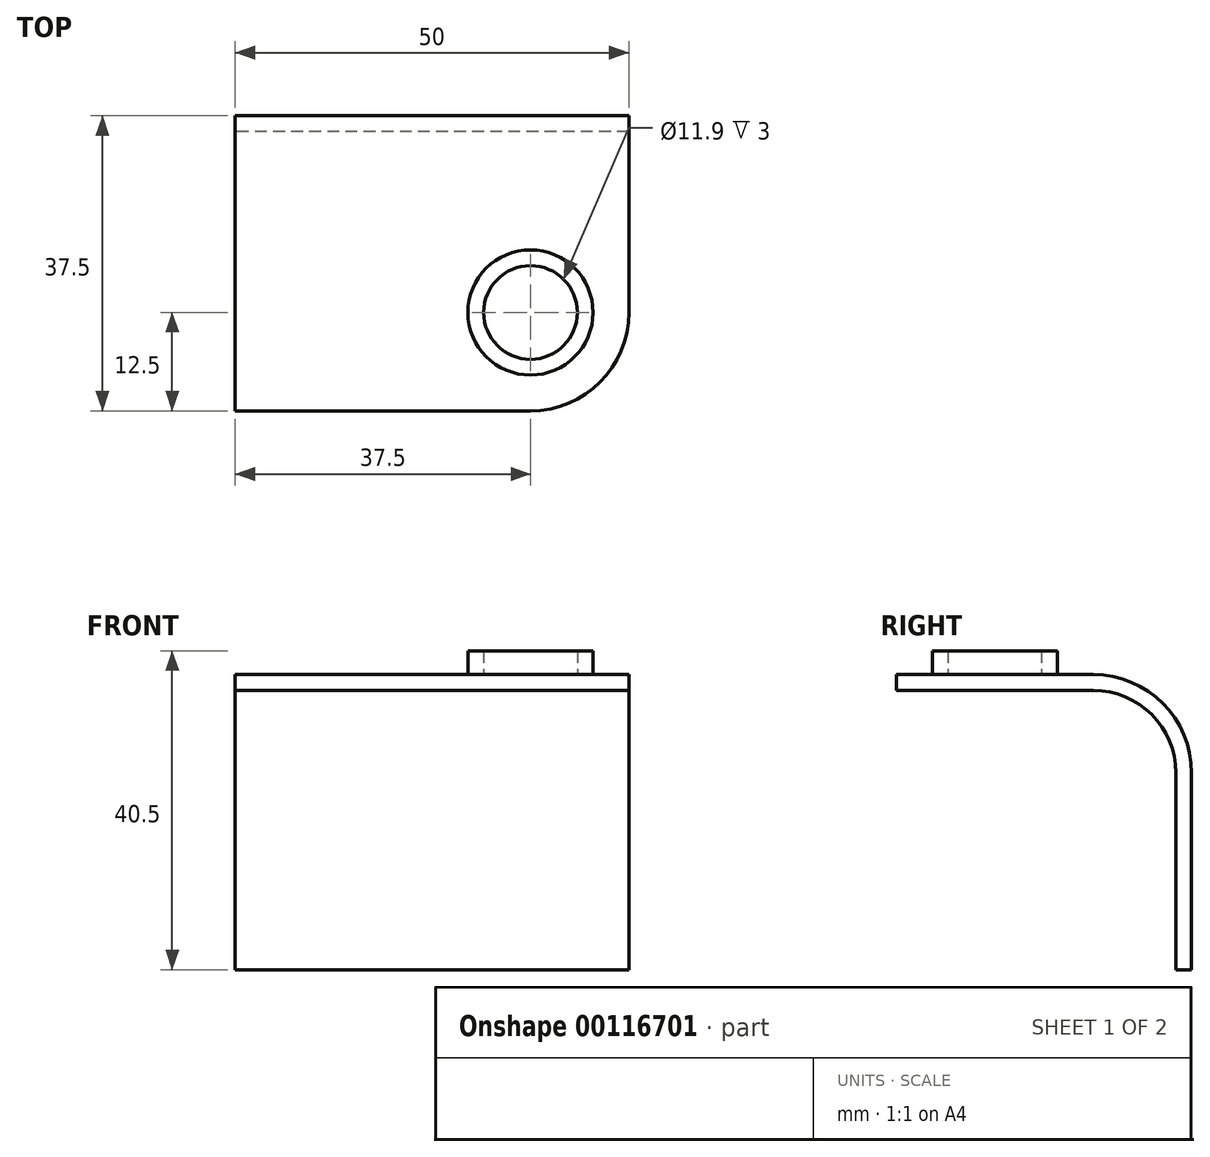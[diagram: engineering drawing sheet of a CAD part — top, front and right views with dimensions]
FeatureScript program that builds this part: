
annotation { "Feature Type Name" : "Feature", "Feature Type Description" : "" }
export const myFeature = defineFeature(function(context is Context, id is Id, definition is map)
    precondition{}
    {
        {
            var Q0;
            Q0=qCreatedBy(makeId("Front.planeOp"),FACE);
            var sketch = newSketch(context, id + "F0", { "sketchPlane" : qUnion([Q0])});
            skLineSegment(sketch, "E0.bottom", {"start": v(0, 0) * mm, "end": v(-50, 0) * mm});
            skLineSegment(sketch, "E0.top", {"start": v(0, 25) * mm, "end": v(-50, 25) * mm});
            skLineSegment(sketch, "E0.left", {"start": v(0, 0) * mm, "end": v(0, 25) * mm});
            skLineSegment(sketch, "E0.right", {"start": v(-50, 0) * mm, "end": v(-50, 25) * mm});
            skSolve(sketch);
        }
        {
            var Q0;
            Q0 = qSketchRegion(id + "F0", true);
            extrude(context, id + "F1", {"entities" : qUnion([Q0]), "depth" : 2 * mm});
        }
        {
            var Q0;
            Q0=qCreatedBy(makeId("Right.planeOp"),FACE);
            var sketch = newSketch(context, id + "F2", { "sketchPlane" : qUnion([Q0])});
            skArc(sketch, "E1", {"start": v(0, 25) * mm, "mid": v(-3.66, 33.84) * mm, "end": v(-12.5, 37.5) * mm});
            skLineSegment(sketch, "E2", {"start": v(-12.5, 37.5) * mm, "end": v(-37.5, 37.5) * mm});
            skLineSegment(sketch, "E3.0", {"start": v(-12.5, 35.5) * mm, "end": v(-37.5, 35.5) * mm});
            skArc(sketch, "E3.1", {"start": v(-2, 25) * mm, "mid": v(-5.08, 32.42) * mm, "end": v(-12.5, 35.5) * mm});
            skLineSegment(sketch, "E4", {"start": v(0, 25) * mm, "end": v(-2, 25) * mm});
            skLineSegment(sketch, "E5", {"start": v(-37.5, 37.5) * mm, "end": v(-37.5, 35.5) * mm});
            skSolve(sketch);
        }
        {
            var Q0;
            Q0=makeQuery(id+"F2.imprint","IMPRINT",FACE,{"disambiguationData":[TD([[makeQuery(id+"F2.imprint","IMPRINT",EDGE,{"derivedFrom":sQuery(id+"F2.wireOp",EDGE,"E1")}),1.0]])]});
            var Q1;
            Q1=makeQuery(id+"F1.opExtrude","SWEPT_FACE",FACE,{"disambiguationData":[OSD([sQuery(id+"F0.wireOp",EDGE,"E0.right")])]});
            extrude(context, id + "F3", {"entities" : qUnion([Q0]), "operationType" : NewBodyOperationType.ADD, "endBound" : BoundingType.UP_TO_SURFACE, "oppositeDirection" : true, "endBoundEntityFace" : qUnion([Q1]), "depth" : 25 * mm});
        }
        {
            var Q0;
            Q0=makeQuery(id+"F3.opExtrude","TWEAK_EDGE",EDGE,{"derivedFrom":[makeQuery(id+"F1.opExtrude","SWEPT_FACE",FACE,{"disambiguationData":[OSD([sQuery(id+"F0.wireOp",EDGE,"E0.right")])]}),makeQuery(id+"F2.imprint","IMPRINT",EDGE,{"derivedFrom":sQuery(id+"F2.wireOp",EDGE,"E5")})]});
            var Q1;
            Q1=makeQuery(id+"F3.opExtrude","CAP_EDGE",EDGE,{"disambiguationData":[OSD([sQuery(id+"F2.wireOp",EDGE,"E5")])],"isStart":true});
            fillet(context, id + "F4", {"entities" : qUnion([Q0, Q1]), "radius" : 12.5 * mm, "tangentPropagation" : true, "allowEdgeOverflow" : false});
        }
        {
            var Q0;
            Q0=makeQuery(id+"F3.opExtrude","SWEPT_FACE",FACE,{"disambiguationData":[OSD([sQuery(id+"F2.wireOp",EDGE,"E2")])]});
            var sketch = newSketch(context, id + "F5", { "sketchPlane" : qUnion([Q0])});
            skCircle(sketch, "E6", {"center": v(-12.5, -25) * mm, "radius": 7.95 * mm});
            skCircle(sketch, "E7.0", {"center": v(-12.5, -25) * mm, "radius": 5.95 * mm});
            skSolve(sketch);
        }
        {
            var Q0;
            Q0 = qSketchRegion(id + "F5", true);
            extrude(context, id + "F6", {"entities" : qUnion([Q0]), "operationType" : NewBodyOperationType.ADD, "depth" : 3 * mm});
        }
    });
